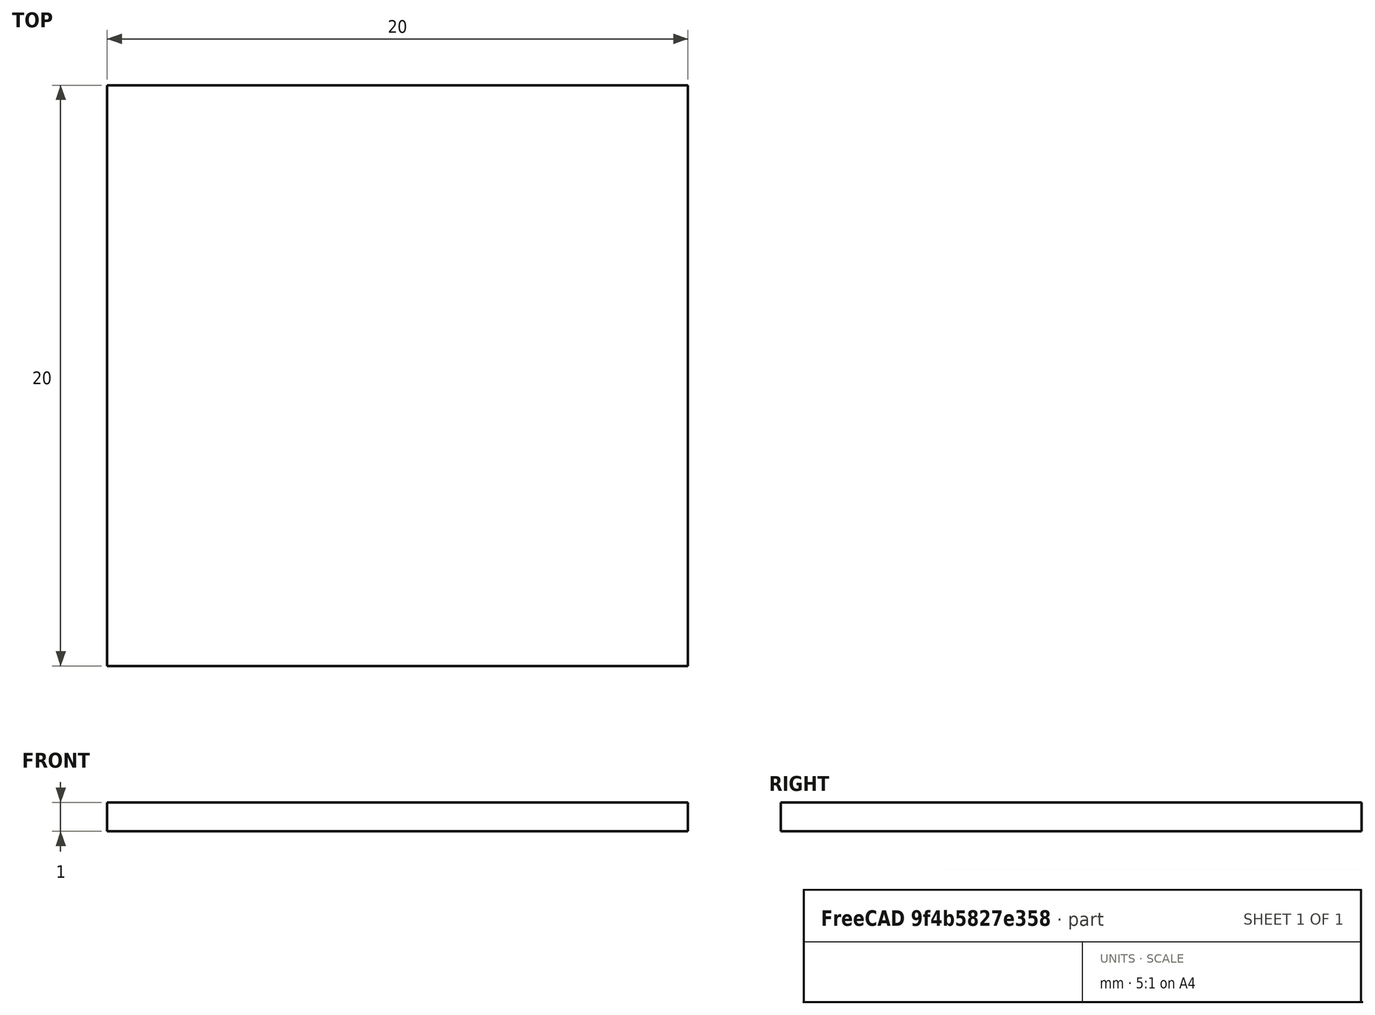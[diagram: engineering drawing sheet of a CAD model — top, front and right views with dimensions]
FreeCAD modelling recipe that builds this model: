
FCSTD DOCUMENT  (FreeCAD 0.16R6712 (Git))
Label: Plaque de test
License: All rights reserved
LicenseURL: http://en.wikipedia.org/wiki/All_rights_reserved
objects: Sketcher::SketchObject×1, PartDesign::Pad×1
note: 3 computed .brp shape members not serialized (recipe doc carries the construction recipe); baked Part::Feature solids carry a one-line shape summary decoded from their .brp

FEATURE [Sketcher::SketchObject] Sketch
  sketch-geometry (4):
    g0: LineSegment StartX=-10 StartY=10 StartZ=0 EndX=10 EndY=10 EndZ=0
    g1: LineSegment StartX=10 StartY=10 StartZ=0 EndX=10 EndY=-10 EndZ=0
    g2: LineSegment StartX=10 StartY=-10 StartZ=0 EndX=-10 EndY=-10 EndZ=0
    g3: LineSegment StartX=-10 StartY=-10 StartZ=0 EndX=-10 EndY=10 EndZ=0
  constraints (12):
    c: Coincident(g0,g1)
    c: Coincident(g1,g2)
    c: Coincident(g2,g3)
    c: Coincident(g3,g0)
    c: Horizontal(g0)
    c: Horizontal(g2)
    c: Vertical(g1)
    c: Vertical(g3)
    c: Symmetric(g2,g0,g-1)
    c: Symmetric(g0,g0,g-2)
    c: DistanceX(g0,g0) = 20
    c: Equal(g0,g3)
FEATURE [PartDesign::Pad] Pad
  Length = 1
  Length2 = 100
  Sketch = -> Sketch
  Type = 0
